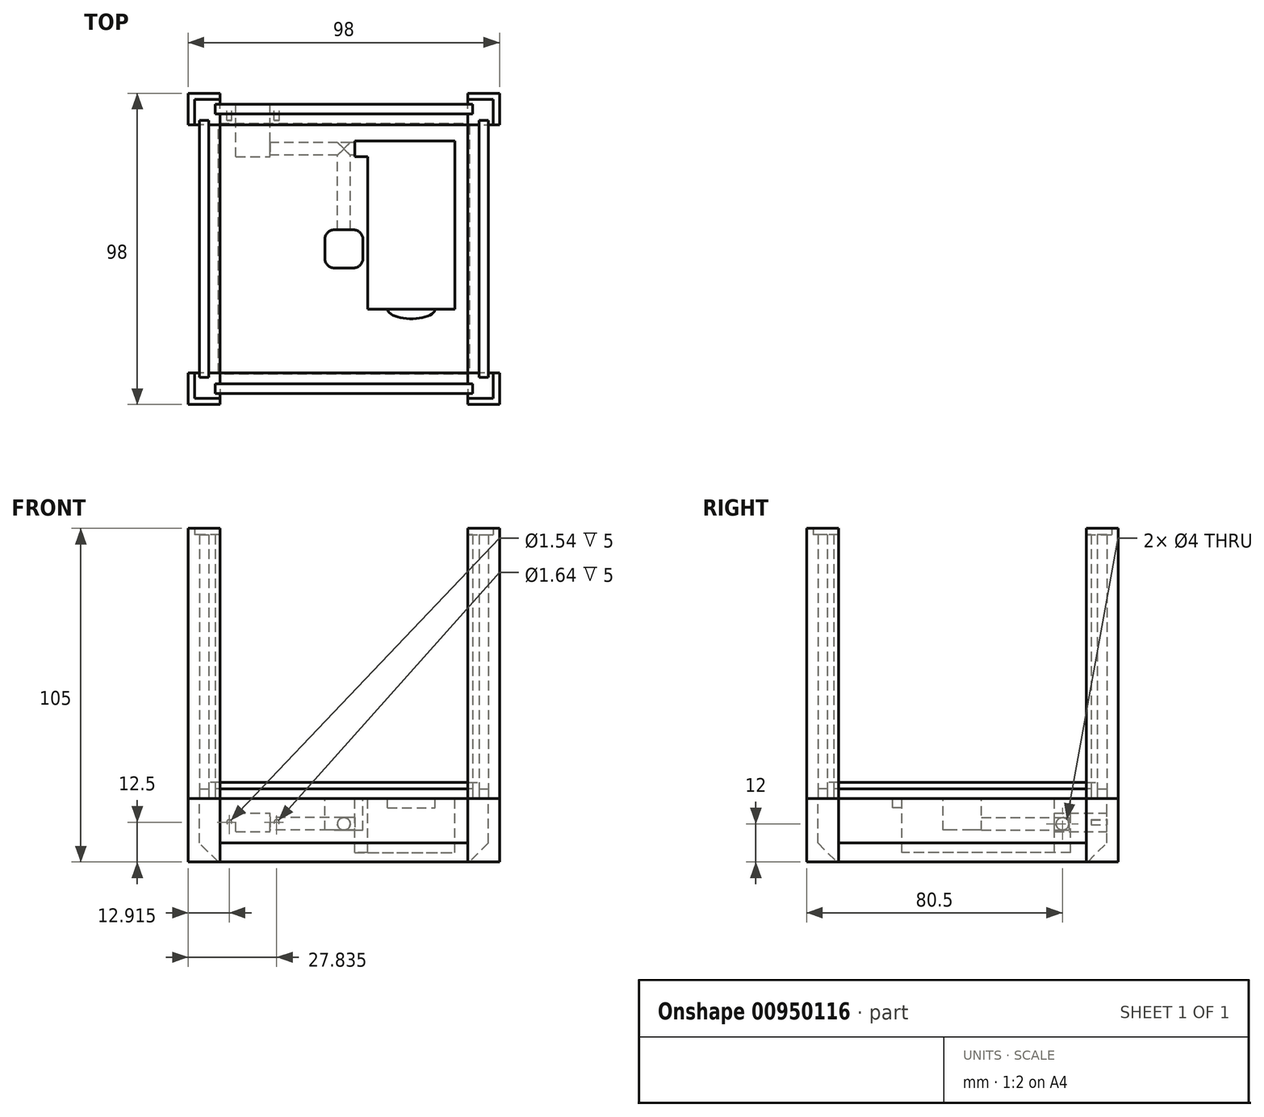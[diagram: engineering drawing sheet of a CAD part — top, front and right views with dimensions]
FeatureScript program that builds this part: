
annotation { "Feature Type Name" : "Feature", "Feature Type Description" : "" }
export const myFeature = defineFeature(function(context is Context, id is Id, definition is map)
    precondition{}
    {
        {
            var Q0;
            Q0=qCreatedBy(makeId("Top.planeOp"),FACE);
            var sketch = newSketch(context, id + "F0", { "sketchPlane" : qUnion([Q0])});
            skLineSegment(sketch, "E0.bottom", {"start": v(44, 44) * mm, "end": v(-44, 44) * mm});
            skLineSegment(sketch, "E0.top", {"start": v(44, -44) * mm, "end": v(-44, -44) * mm});
            skLineSegment(sketch, "E0.left", {"start": v(44, 44) * mm, "end": v(44, -44) * mm});
            skLineSegment(sketch, "E0.right", {"start": v(-44, 44) * mm, "end": v(-44, -44) * mm});
            skPoint(sketch, "E0.middle", {"position": v(0, 0) * mm});
            skLineSegment(sketch, "E1.bottom", {"start": v(39, 39) * mm, "end": v(49, 39) * mm});
            skLineSegment(sketch, "E1.top", {"start": v(39, 49) * mm, "end": v(49, 49) * mm});
            skLineSegment(sketch, "E1.left", {"start": v(39, 39) * mm, "end": v(39, 49) * mm});
            skLineSegment(sketch, "E1.right", {"start": v(49, 39) * mm, "end": v(49, 49) * mm});
            skPoint(sketch, "E1.middle", {"position": v(44, 44) * mm});
            skLineSegment(sketch, "E2.bottom", {"start": v(49, -39) * mm, "end": v(39, -39) * mm});
            skLineSegment(sketch, "E2.top", {"start": v(49, -49) * mm, "end": v(39, -49) * mm});
            skLineSegment(sketch, "E2.left", {"start": v(49, -39) * mm, "end": v(49, -49) * mm});
            skLineSegment(sketch, "E2.right", {"start": v(39, -39) * mm, "end": v(39, -49) * mm});
            skPoint(sketch, "E2.middle", {"position": v(44, -44) * mm});
            skLineSegment(sketch, "E3.bottom", {"start": v(-39, -39) * mm, "end": v(-49, -39) * mm});
            skLineSegment(sketch, "E3.top", {"start": v(-39, -49) * mm, "end": v(-49, -49) * mm});
            skLineSegment(sketch, "E3.left", {"start": v(-39, -39) * mm, "end": v(-39, -49) * mm});
            skLineSegment(sketch, "E3.right", {"start": v(-49, -39) * mm, "end": v(-49, -49) * mm});
            skPoint(sketch, "E3.middle", {"position": v(-44, -44) * mm});
            skLineSegment(sketch, "E4.bottom", {"start": v(-39, 39) * mm, "end": v(-49, 39) * mm});
            skLineSegment(sketch, "E4.top", {"start": v(-39, 49) * mm, "end": v(-49, 49) * mm});
            skLineSegment(sketch, "E4.left", {"start": v(-39, 39) * mm, "end": v(-39, 49) * mm});
            skLineSegment(sketch, "E4.right", {"start": v(-49, 39) * mm, "end": v(-49, 49) * mm});
            skPoint(sketch, "E4.middle", {"position": v(-44, 44) * mm});
            skLineSegment(sketch, "E5.0", {"start": v(45.5, 45.5) * mm, "end": v(45.5, -45.5) * mm});
            skLineSegment(sketch, "E5.1", {"start": v(45.5, 45.5) * mm, "end": v(-45.5, 45.5) * mm});
            skLineSegment(sketch, "E5.2", {"start": v(-45.5, 45.5) * mm, "end": v(-45.5, -45.5) * mm});
            skLineSegment(sketch, "E5.3", {"start": v(45.5, -45.5) * mm, "end": v(-45.5, -45.5) * mm});
            skLineSegment(sketch, "E6.0", {"start": v(42.5, 42.5) * mm, "end": v(42.5, -42.5) * mm});
            skLineSegment(sketch, "E6.1", {"start": v(42.5, 42.5) * mm, "end": v(-42.5, 42.5) * mm});
            skLineSegment(sketch, "E6.2", {"start": v(-42.5, 42.5) * mm, "end": v(-42.5, -42.5) * mm});
            skLineSegment(sketch, "E6.3", {"start": v(42.5, -42.5) * mm, "end": v(-42.5, -42.5) * mm});
            skLineSegment(sketch, "E7", {"start": v(42.5, 40.5) * mm, "end": v(45.5, 40.5) * mm});
            skLineSegment(sketch, "E8", {"start": v(40.5, 45.5) * mm, "end": v(40.5, 42.5) * mm});
            skLineSegment(sketch, "E9", {"start": v(42.5, -40.5) * mm, "end": v(45.5, -40.5) * mm});
            skLineSegment(sketch, "E10", {"start": v(40.5, -42.5) * mm, "end": v(40.5, -45.5) * mm});
            skLineSegment(sketch, "E11", {"start": v(-45.5, -40.5) * mm, "end": v(-42.5, -40.5) * mm});
            skLineSegment(sketch, "E12", {"start": v(-40.5, -42.5) * mm, "end": v(-40.5, -45.5) * mm});
            skLineSegment(sketch, "E13", {"start": v(-45.5, 40.5) * mm, "end": v(-42.5, 40.5) * mm});
            skLineSegment(sketch, "E14", {"start": v(-40.5, 42.5) * mm, "end": v(-40.5, 45.5) * mm});
            skLineSegment(sketch, "E15.0", {"start": v(39, 39) * mm, "end": v(-39, 39) * mm});
            skLineSegment(sketch, "E15.1", {"start": v(39, 39) * mm, "end": v(39, -39) * mm});
            skLineSegment(sketch, "E15.2", {"start": v(39, -39) * mm, "end": v(-39, -39) * mm});
            skLineSegment(sketch, "E15.3", {"start": v(-39, 39) * mm, "end": v(-39, -39) * mm});
            skSolve(sketch);
        }
        {
            var Q0;
            {var subQ0=sQuery(id+"F0.wireOp",EDGE,"E15.3");Q0=makeQuery(id+"F0.imprint","IMPRINT",FACE,{"disambiguationData":[TD([[makeQuery(id+"F0.imprint","IMPRINT",EDGE,{"derivedFrom":subQ0}),-1.0]])]});}
            var Q1;
            {var subQ0=sQuery(id+"F0.wireOp",EDGE,"E15.0");Q1=makeQuery(id+"F0.imprint","IMPRINT",FACE,{"disambiguationData":[TD([[makeQuery(id+"F0.imprint","IMPRINT",EDGE,{"derivedFrom":subQ0}),-1.0]])]});}
            var Q2;
            {var subQ0=sQuery(id+"F0.wireOp",EDGE,"E15.1");Q2=makeQuery(id+"F0.imprint","IMPRINT",FACE,{"disambiguationData":[TD([[makeQuery(id+"F0.imprint","IMPRINT",EDGE,{"derivedFrom":subQ0}),1.0]])]});}
            var Q3;
            {var subQ0=sQuery(id+"F0.wireOp",EDGE,"E15.2");Q3=makeQuery(id+"F0.imprint","IMPRINT",FACE,{"disambiguationData":[TD([[makeQuery(id+"F0.imprint","IMPRINT",EDGE,{"derivedFrom":subQ0}),1.0]])]});}
            extrude(context, id + "F1", {"entities" : qUnion([Q0, Q1, Q2, Q3]), "depth" : 5 * mm, "offsetDistance" : 25 * mm});
        }
        {
            var Q0;
            {var subQ1=sQuery(id+"F0.wireOp",EDGE,"E6.1");var subQ3=makeQuery(id+"F0.imprint","INTERSECT",VERTEX,{"derivedFrom":[subQ1,sQuery(id+"F0.wireOp",EDGE,"E14")]});Q0=makeQuery(id+"F0.imprint","IMPRINT",FACE,{"disambiguationData":[TD([[makeQuery(id+"F0.imprint","IMPRINT",EDGE,{"disambiguationData":[TD([[subQ3,1.0]])],"derivedFrom":subQ1}),1.0]])]});}
            var Q1;
            {var subQ5=sQuery(id+"F0.wireOp",EDGE,"E0.right");var subQ6=sQuery(id+"F0.wireOp",EDGE,"E0.bottom");var subQ7=makeQuery(id+"F0.imprint","INTERSECT",VERTEX,{"derivedFrom":[subQ6,subQ5]});Q1=makeQuery(id+"F0.imprint","IMPRINT",FACE,{"disambiguationData":[TD([[makeQuery(id+"F0.imprint","IMPRINT",EDGE,{"disambiguationData":[TD([[subQ7,1.0]])],"derivedFrom":subQ6}),1.0]])]});}
            var Q2;
            {var subQ5=sQuery(id+"F0.wireOp",EDGE,"E0.right");var subQ6=sQuery(id+"F0.wireOp",EDGE,"E0.bottom");var subQ7=makeQuery(id+"F0.imprint","INTERSECT",VERTEX,{"derivedFrom":[subQ6,subQ5]});Q2=makeQuery(id+"F0.imprint","IMPRINT",FACE,{"disambiguationData":[TD([[makeQuery(id+"F0.imprint","IMPRINT",EDGE,{"disambiguationData":[TD([[subQ7,1.0]])],"derivedFrom":subQ6}),-1.0]])]});}
            var Q3;
            {var subQ5=sQuery(id+"F0.wireOp",EDGE,"E4.top");Q3=makeQuery(id+"F0.imprint","IMPRINT",FACE,{"disambiguationData":[TD([[makeQuery(id+"F0.imprint","IMPRINT",EDGE,{"derivedFrom":subQ5}),1.0]])]});}
            var Q4;
            {var subQ1=sQuery(id+"F0.wireOp",EDGE,"E1.top");Q4=makeQuery(id+"F0.imprint","IMPRINT",FACE,{"disambiguationData":[TD([[makeQuery(id+"F0.imprint","IMPRINT",EDGE,{"derivedFrom":subQ1}),-1.0]])]});}
            var Q5;
            {var subQ5=sQuery(id+"F0.wireOp",EDGE,"E0.left");var subQ6=sQuery(id+"F0.wireOp",EDGE,"E0.bottom");var subQ7=makeQuery(id+"F0.imprint","INTERSECT",VERTEX,{"derivedFrom":[subQ6,subQ5]});Q5=makeQuery(id+"F0.imprint","IMPRINT",FACE,{"disambiguationData":[TD([[makeQuery(id+"F0.imprint","IMPRINT",EDGE,{"disambiguationData":[TD([[subQ7,-1.0]])],"derivedFrom":subQ6}),-1.0]])]});}
            var Q6;
            {var subQ7=sQuery(id+"F0.wireOp",EDGE,"E0.left");var subQ8=sQuery(id+"F0.wireOp",EDGE,"E0.bottom");var subQ9=makeQuery(id+"F0.imprint","INTERSECT",VERTEX,{"derivedFrom":[subQ8,subQ7]});Q6=makeQuery(id+"F0.imprint","IMPRINT",FACE,{"disambiguationData":[TD([[makeQuery(id+"F0.imprint","IMPRINT",EDGE,{"disambiguationData":[TD([[subQ9,-1.0]])],"derivedFrom":subQ8}),1.0]])]});}
            var Q7;
            {var subQ0=sQuery(id+"F0.wireOp",EDGE,"E6.0");var subQ4=sQuery(id+"F0.wireOp",EDGE,"E6.1");var subQ5=makeQuery(id+"F0.imprint","INTERSECT",VERTEX,{"derivedFrom":[subQ0,subQ4]});Q7=makeQuery(id+"F0.imprint","IMPRINT",FACE,{"disambiguationData":[TD([[makeQuery(id+"F0.imprint","IMPRINT",EDGE,{"disambiguationData":[TD([[subQ5,-1.0]])],"derivedFrom":subQ0}),-1.0]])]});}
            var Q8;
            {var subQ1=sQuery(id+"F0.wireOp",EDGE,"E2.top");Q8=makeQuery(id+"F0.imprint","IMPRINT",FACE,{"disambiguationData":[TD([[makeQuery(id+"F0.imprint","IMPRINT",EDGE,{"derivedFrom":subQ1}),-1.0]])]});}
            var Q9;
            {var subQ7=sQuery(id+"F0.wireOp",EDGE,"E0.left");var subQ8=sQuery(id+"F0.wireOp",EDGE,"E0.top");var subQ9=makeQuery(id+"F0.imprint","INTERSECT",VERTEX,{"derivedFrom":[subQ8,subQ7]});Q9=makeQuery(id+"F0.imprint","IMPRINT",FACE,{"disambiguationData":[TD([[makeQuery(id+"F0.imprint","IMPRINT",EDGE,{"disambiguationData":[TD([[subQ9,-1.0]])],"derivedFrom":subQ8}),1.0]])]});}
            var Q10;
            {var subQ7=sQuery(id+"F0.wireOp",EDGE,"E0.top");var subQ9=sQuery(id+"F0.wireOp",EDGE,"E0.left");var subQ10=makeQuery(id+"F0.imprint","INTERSECT",VERTEX,{"derivedFrom":[subQ7,subQ9]});Q10=makeQuery(id+"F0.imprint","IMPRINT",FACE,{"disambiguationData":[TD([[makeQuery(id+"F0.imprint","IMPRINT",EDGE,{"disambiguationData":[TD([[subQ10,-1.0]])],"derivedFrom":subQ7}),-1.0]])]});}
            var Q11;
            {var subQ1=sQuery(id+"F0.wireOp",EDGE,"E6.0");var subQ3=makeQuery(id+"F0.imprint","INTERSECT",VERTEX,{"derivedFrom":[subQ1,sQuery(id+"F0.wireOp",EDGE,"E9")]});Q11=makeQuery(id+"F0.imprint","IMPRINT",FACE,{"disambiguationData":[TD([[makeQuery(id+"F0.imprint","IMPRINT",EDGE,{"disambiguationData":[TD([[subQ3,1.0]])],"derivedFrom":subQ1}),-1.0]])]});}
            var Q12;
            {var subQ1=sQuery(id+"F0.wireOp",EDGE,"E6.2");var subQ3=makeQuery(id+"F0.imprint","INTERSECT",VERTEX,{"derivedFrom":[subQ1,sQuery(id+"F0.wireOp",EDGE,"E11")]});Q12=makeQuery(id+"F0.imprint","IMPRINT",FACE,{"disambiguationData":[TD([[makeQuery(id+"F0.imprint","IMPRINT",EDGE,{"disambiguationData":[TD([[subQ3,1.0]])],"derivedFrom":subQ1}),1.0]])]});}
            var Q13;
            {var subQ5=sQuery(id+"F0.wireOp",EDGE,"E0.top");var subQ9=sQuery(id+"F0.wireOp",EDGE,"E0.right");var subQ10=makeQuery(id+"F0.imprint","INTERSECT",VERTEX,{"derivedFrom":[subQ5,subQ9]});Q13=makeQuery(id+"F0.imprint","IMPRINT",FACE,{"disambiguationData":[TD([[makeQuery(id+"F0.imprint","IMPRINT",EDGE,{"disambiguationData":[TD([[subQ10,1.0]])],"derivedFrom":subQ5}),-1.0]])]});}
            var Q14;
            {var subQ7=sQuery(id+"F0.wireOp",EDGE,"E0.right");var subQ8=sQuery(id+"F0.wireOp",EDGE,"E0.top");var subQ9=makeQuery(id+"F0.imprint","INTERSECT",VERTEX,{"derivedFrom":[subQ8,subQ7]});Q14=makeQuery(id+"F0.imprint","IMPRINT",FACE,{"disambiguationData":[TD([[makeQuery(id+"F0.imprint","IMPRINT",EDGE,{"disambiguationData":[TD([[subQ9,1.0]])],"derivedFrom":subQ8}),1.0]])]});}
            var Q15;
            {var subQ1=sQuery(id+"F0.wireOp",EDGE,"E3.top");Q15=makeQuery(id+"F0.imprint","IMPRINT",FACE,{"disambiguationData":[TD([[makeQuery(id+"F0.imprint","IMPRINT",EDGE,{"derivedFrom":subQ1}),-1.0]])]});}
            extrude(context, id + "F2", {"entities" : qUnion([Q0, Q1, Q2, Q3, Q4, Q5, Q6, Q7, Q8, Q9, Q10, Q11, Q12, Q13, Q14, Q15]), "depth" : 83 * mm, "offsetDistance" : 25 * mm});
        }
        {
            var Q0;
            {var subQ0=sQuery(id+"F0.wireOp",EDGE,"E4.bottom");var subQ1=sQuery(id+"F0.wireOp",EDGE,"E0.right");var subQ2=makeQuery(id+"F0.imprint","INTERSECT",VERTEX,{"derivedFrom":[subQ1,subQ0]});Q0=makeQuery(id+"F0.imprint","IMPRINT",FACE,{"disambiguationData":[TD([[makeQuery(id+"F0.imprint","IMPRINT",EDGE,{"disambiguationData":[TD([[subQ2,-1.0]])],"derivedFrom":subQ1}),1.0]])]});}
            var Q1;
            {var subQ0=sQuery(id+"F0.wireOp",EDGE,"E4.bottom");var subQ1=sQuery(id+"F0.wireOp",EDGE,"E0.right");var subQ2=makeQuery(id+"F0.imprint","INTERSECT",VERTEX,{"derivedFrom":[subQ1,subQ0]});Q1=makeQuery(id+"F0.imprint","IMPRINT",FACE,{"disambiguationData":[TD([[makeQuery(id+"F0.imprint","IMPRINT",EDGE,{"disambiguationData":[TD([[subQ2,-1.0]])],"derivedFrom":subQ1}),-1.0]])]});}
            var Q2;
            {var subQ0=sQuery(id+"F0.wireOp",EDGE,"E13");var subQ1=sQuery(id+"F0.wireOp",EDGE,"E0.right");var subQ2=makeQuery(id+"F0.imprint","INTERSECT",VERTEX,{"derivedFrom":[subQ1,subQ0]});Q2=makeQuery(id+"F0.imprint","IMPRINT",FACE,{"disambiguationData":[TD([[makeQuery(id+"F0.imprint","IMPRINT",EDGE,{"disambiguationData":[TD([[subQ2,-1.0]])],"derivedFrom":subQ1}),1.0]])]});}
            var Q3;
            {var subQ0=sQuery(id+"F0.wireOp",EDGE,"E13");var subQ1=sQuery(id+"F0.wireOp",EDGE,"E0.right");var subQ2=makeQuery(id+"F0.imprint","INTERSECT",VERTEX,{"derivedFrom":[subQ1,subQ0]});Q3=makeQuery(id+"F0.imprint","IMPRINT",FACE,{"disambiguationData":[TD([[makeQuery(id+"F0.imprint","IMPRINT",EDGE,{"disambiguationData":[TD([[subQ2,-1.0]])],"derivedFrom":subQ1}),-1.0]])]});}
            var Q4;
            {var subQ0=sQuery(id+"F0.wireOp",EDGE,"E3.bottom");var subQ1=sQuery(id+"F0.wireOp",EDGE,"E0.right");var subQ2=makeQuery(id+"F0.imprint","INTERSECT",VERTEX,{"derivedFrom":[subQ1,subQ0]});Q4=makeQuery(id+"F0.imprint","IMPRINT",FACE,{"disambiguationData":[TD([[makeQuery(id+"F0.imprint","IMPRINT",EDGE,{"disambiguationData":[TD([[subQ2,-1.0]])],"derivedFrom":subQ1}),1.0]])]});}
            var Q5;
            {var subQ0=sQuery(id+"F0.wireOp",EDGE,"E3.bottom");var subQ1=sQuery(id+"F0.wireOp",EDGE,"E0.right");var subQ2=makeQuery(id+"F0.imprint","INTERSECT",VERTEX,{"derivedFrom":[subQ1,subQ0]});Q5=makeQuery(id+"F0.imprint","IMPRINT",FACE,{"disambiguationData":[TD([[makeQuery(id+"F0.imprint","IMPRINT",EDGE,{"disambiguationData":[TD([[subQ2,-1.0]])],"derivedFrom":subQ1}),-1.0]])]});}
            var Q6;
            {var subQ0=sQuery(id+"F0.wireOp",EDGE,"E2.right");var subQ1=sQuery(id+"F0.wireOp",EDGE,"E0.top");var subQ2=makeQuery(id+"F0.imprint","INTERSECT",VERTEX,{"derivedFrom":[subQ1,subQ0]});Q6=makeQuery(id+"F0.imprint","IMPRINT",FACE,{"disambiguationData":[TD([[makeQuery(id+"F0.imprint","IMPRINT",EDGE,{"disambiguationData":[TD([[subQ2,-1.0]])],"derivedFrom":subQ1}),-1.0]])]});}
            var Q7;
            {var subQ0=sQuery(id+"F0.wireOp",EDGE,"E3.left");var subQ1=sQuery(id+"F0.wireOp",EDGE,"E0.top");var subQ2=makeQuery(id+"F0.imprint","INTERSECT",VERTEX,{"derivedFrom":[subQ1,subQ0]});Q7=makeQuery(id+"F0.imprint","IMPRINT",FACE,{"disambiguationData":[TD([[makeQuery(id+"F0.imprint","IMPRINT",EDGE,{"disambiguationData":[TD([[subQ2,-1.0]])],"derivedFrom":subQ1}),-1.0]])]});}
            var Q8;
            {var subQ0=sQuery(id+"F0.wireOp",EDGE,"E3.left");var subQ1=sQuery(id+"F0.wireOp",EDGE,"E0.top");var subQ2=makeQuery(id+"F0.imprint","INTERSECT",VERTEX,{"derivedFrom":[subQ1,subQ0]});Q8=makeQuery(id+"F0.imprint","IMPRINT",FACE,{"disambiguationData":[TD([[makeQuery(id+"F0.imprint","IMPRINT",EDGE,{"disambiguationData":[TD([[subQ2,-1.0]])],"derivedFrom":subQ1}),1.0]])]});}
            var Q9;
            {var subQ0=sQuery(id+"F0.wireOp",EDGE,"E2.right");var subQ1=sQuery(id+"F0.wireOp",EDGE,"E0.top");var subQ2=makeQuery(id+"F0.imprint","INTERSECT",VERTEX,{"derivedFrom":[subQ1,subQ0]});Q9=makeQuery(id+"F0.imprint","IMPRINT",FACE,{"disambiguationData":[TD([[makeQuery(id+"F0.imprint","IMPRINT",EDGE,{"disambiguationData":[TD([[subQ2,-1.0]])],"derivedFrom":subQ1}),1.0]])]});}
            var Q10;
            {var subQ0=sQuery(id+"F0.wireOp",EDGE,"E10");var subQ1=sQuery(id+"F0.wireOp",EDGE,"E0.top");var subQ2=makeQuery(id+"F0.imprint","INTERSECT",VERTEX,{"derivedFrom":[subQ1,subQ0]});Q10=makeQuery(id+"F0.imprint","IMPRINT",FACE,{"disambiguationData":[TD([[makeQuery(id+"F0.imprint","IMPRINT",EDGE,{"disambiguationData":[TD([[subQ2,-1.0]])],"derivedFrom":subQ1}),1.0]])]});}
            var Q11;
            {var subQ0=sQuery(id+"F0.wireOp",EDGE,"E10");var subQ1=sQuery(id+"F0.wireOp",EDGE,"E0.top");var subQ2=makeQuery(id+"F0.imprint","INTERSECT",VERTEX,{"derivedFrom":[subQ1,subQ0]});Q11=makeQuery(id+"F0.imprint","IMPRINT",FACE,{"disambiguationData":[TD([[makeQuery(id+"F0.imprint","IMPRINT",EDGE,{"disambiguationData":[TD([[subQ2,-1.0]])],"derivedFrom":subQ1}),-1.0]])]});}
            var Q12;
            {var subQ0=sQuery(id+"F0.wireOp",EDGE,"E2.bottom");var subQ1=sQuery(id+"F0.wireOp",EDGE,"E0.left");var subQ2=makeQuery(id+"F0.imprint","INTERSECT",VERTEX,{"derivedFrom":[subQ1,subQ0]});Q12=makeQuery(id+"F0.imprint","IMPRINT",FACE,{"disambiguationData":[TD([[makeQuery(id+"F0.imprint","IMPRINT",EDGE,{"disambiguationData":[TD([[subQ2,-1.0]])],"derivedFrom":subQ1}),-1.0]])]});}
            var Q13;
            {var subQ0=sQuery(id+"F0.wireOp",EDGE,"E2.bottom");var subQ1=sQuery(id+"F0.wireOp",EDGE,"E0.left");var subQ2=makeQuery(id+"F0.imprint","INTERSECT",VERTEX,{"derivedFrom":[subQ1,subQ0]});Q13=makeQuery(id+"F0.imprint","IMPRINT",FACE,{"disambiguationData":[TD([[makeQuery(id+"F0.imprint","IMPRINT",EDGE,{"disambiguationData":[TD([[subQ2,-1.0]])],"derivedFrom":subQ1}),1.0]])]});}
            var Q14;
            {var subQ0=sQuery(id+"F0.wireOp",EDGE,"E1.bottom");var subQ1=sQuery(id+"F0.wireOp",EDGE,"E0.left");var subQ2=makeQuery(id+"F0.imprint","INTERSECT",VERTEX,{"derivedFrom":[subQ1,subQ0]});Q14=makeQuery(id+"F0.imprint","IMPRINT",FACE,{"disambiguationData":[TD([[makeQuery(id+"F0.imprint","IMPRINT",EDGE,{"disambiguationData":[TD([[subQ2,-1.0]])],"derivedFrom":subQ1}),1.0]])]});}
            var Q15;
            {var subQ0=sQuery(id+"F0.wireOp",EDGE,"E1.bottom");var subQ1=sQuery(id+"F0.wireOp",EDGE,"E0.left");var subQ2=makeQuery(id+"F0.imprint","INTERSECT",VERTEX,{"derivedFrom":[subQ1,subQ0]});Q15=makeQuery(id+"F0.imprint","IMPRINT",FACE,{"disambiguationData":[TD([[makeQuery(id+"F0.imprint","IMPRINT",EDGE,{"disambiguationData":[TD([[subQ2,-1.0]])],"derivedFrom":subQ1}),-1.0]])]});}
            var Q16;
            {var subQ0=sQuery(id+"F0.wireOp",EDGE,"E7");var subQ1=sQuery(id+"F0.wireOp",EDGE,"E0.left");var subQ2=makeQuery(id+"F0.imprint","INTERSECT",VERTEX,{"derivedFrom":[subQ1,subQ0]});Q16=makeQuery(id+"F0.imprint","IMPRINT",FACE,{"disambiguationData":[TD([[makeQuery(id+"F0.imprint","IMPRINT",EDGE,{"disambiguationData":[TD([[subQ2,-1.0]])],"derivedFrom":subQ1}),1.0]])]});}
            var Q17;
            {var subQ0=sQuery(id+"F0.wireOp",EDGE,"E7");var subQ1=sQuery(id+"F0.wireOp",EDGE,"E0.left");var subQ2=makeQuery(id+"F0.imprint","INTERSECT",VERTEX,{"derivedFrom":[subQ1,subQ0]});Q17=makeQuery(id+"F0.imprint","IMPRINT",FACE,{"disambiguationData":[TD([[makeQuery(id+"F0.imprint","IMPRINT",EDGE,{"disambiguationData":[TD([[subQ2,-1.0]])],"derivedFrom":subQ1}),-1.0]])]});}
            var Q18;
            {var subQ0=sQuery(id+"F0.wireOp",EDGE,"E8");var subQ1=sQuery(id+"F0.wireOp",EDGE,"E0.bottom");var subQ2=makeQuery(id+"F0.imprint","INTERSECT",VERTEX,{"derivedFrom":[subQ1,subQ0]});Q18=makeQuery(id+"F0.imprint","IMPRINT",FACE,{"disambiguationData":[TD([[makeQuery(id+"F0.imprint","IMPRINT",EDGE,{"disambiguationData":[TD([[subQ2,-1.0]])],"derivedFrom":subQ1}),1.0]])]});}
            var Q19;
            {var subQ0=sQuery(id+"F0.wireOp",EDGE,"E8");var subQ1=sQuery(id+"F0.wireOp",EDGE,"E0.bottom");var subQ2=makeQuery(id+"F0.imprint","INTERSECT",VERTEX,{"derivedFrom":[subQ1,subQ0]});Q19=makeQuery(id+"F0.imprint","IMPRINT",FACE,{"disambiguationData":[TD([[makeQuery(id+"F0.imprint","IMPRINT",EDGE,{"disambiguationData":[TD([[subQ2,-1.0]])],"derivedFrom":subQ1}),-1.0]])]});}
            var Q20;
            {var subQ0=sQuery(id+"F0.wireOp",EDGE,"E1.left");var subQ1=sQuery(id+"F0.wireOp",EDGE,"E0.bottom");var subQ2=makeQuery(id+"F0.imprint","INTERSECT",VERTEX,{"derivedFrom":[subQ1,subQ0]});Q20=makeQuery(id+"F0.imprint","IMPRINT",FACE,{"disambiguationData":[TD([[makeQuery(id+"F0.imprint","IMPRINT",EDGE,{"disambiguationData":[TD([[subQ2,-1.0]])],"derivedFrom":subQ1}),-1.0]])]});}
            var Q21;
            {var subQ0=sQuery(id+"F0.wireOp",EDGE,"E1.left");var subQ1=sQuery(id+"F0.wireOp",EDGE,"E0.bottom");var subQ2=makeQuery(id+"F0.imprint","INTERSECT",VERTEX,{"derivedFrom":[subQ1,subQ0]});Q21=makeQuery(id+"F0.imprint","IMPRINT",FACE,{"disambiguationData":[TD([[makeQuery(id+"F0.imprint","IMPRINT",EDGE,{"disambiguationData":[TD([[subQ2,-1.0]])],"derivedFrom":subQ1}),1.0]])]});}
            var Q22;
            {var subQ0=sQuery(id+"F0.wireOp",EDGE,"E4.left");var subQ1=sQuery(id+"F0.wireOp",EDGE,"E0.bottom");var subQ2=makeQuery(id+"F0.imprint","INTERSECT",VERTEX,{"derivedFrom":[subQ1,subQ0]});Q22=makeQuery(id+"F0.imprint","IMPRINT",FACE,{"disambiguationData":[TD([[makeQuery(id+"F0.imprint","IMPRINT",EDGE,{"disambiguationData":[TD([[subQ2,-1.0]])],"derivedFrom":subQ1}),1.0]])]});}
            var Q23;
            {var subQ0=sQuery(id+"F0.wireOp",EDGE,"E4.left");var subQ1=sQuery(id+"F0.wireOp",EDGE,"E0.bottom");var subQ2=makeQuery(id+"F0.imprint","INTERSECT",VERTEX,{"derivedFrom":[subQ1,subQ0]});Q23=makeQuery(id+"F0.imprint","IMPRINT",FACE,{"disambiguationData":[TD([[makeQuery(id+"F0.imprint","IMPRINT",EDGE,{"disambiguationData":[TD([[subQ2,-1.0]])],"derivedFrom":subQ1}),-1.0]])]});}
            extrude(context, id + "F3", {"entities" : qUnion([Q0, Q1, Q2, Q3, Q4, Q5, Q6, Q7, Q8, Q9, Q10, Q11, Q12, Q13, Q14, Q15, Q16, Q17, Q18, Q19, Q20, Q21, Q22, Q23]), "depth" : 3 * mm, "offsetDistance" : 25 * mm});
        }
        {
            var Q0;
            {var subQ0=sQuery(id+"F0.wireOp",EDGE,"E1.left");var subQ1=sQuery(id+"F0.wireOp",EDGE,"E0.bottom");var subQ2=makeQuery(id+"F0.imprint","INTERSECT",VERTEX,{"derivedFrom":[subQ1,subQ0]});Q0=makeQuery(id+"F0.imprint","IMPRINT",FACE,{"disambiguationData":[TD([[makeQuery(id+"F0.imprint","IMPRINT",EDGE,{"disambiguationData":[TD([[subQ2,-1.0]])],"derivedFrom":subQ1}),-1.0]])]});}
            var Q1;
            {var subQ0=sQuery(id+"F0.wireOp",EDGE,"E2.right");var subQ1=sQuery(id+"F0.wireOp",EDGE,"E0.top");var subQ2=makeQuery(id+"F0.imprint","INTERSECT",VERTEX,{"derivedFrom":[subQ1,subQ0]});Q1=makeQuery(id+"F0.imprint","IMPRINT",FACE,{"disambiguationData":[TD([[makeQuery(id+"F0.imprint","IMPRINT",EDGE,{"disambiguationData":[TD([[subQ2,-1.0]])],"derivedFrom":subQ1}),1.0]])]});}
            var Q2;
            {var subQ0=sQuery(id+"F0.wireOp",EDGE,"E1.bottom");var subQ1=sQuery(id+"F0.wireOp",EDGE,"E0.left");var subQ2=makeQuery(id+"F0.imprint","INTERSECT",VERTEX,{"derivedFrom":[subQ1,subQ0]});Q2=makeQuery(id+"F0.imprint","IMPRINT",FACE,{"disambiguationData":[TD([[makeQuery(id+"F0.imprint","IMPRINT",EDGE,{"disambiguationData":[TD([[subQ2,-1.0]])],"derivedFrom":subQ1}),1.0]])]});}
            var Q3;
            {var subQ0=sQuery(id+"F0.wireOp",EDGE,"E4.bottom");var subQ1=sQuery(id+"F0.wireOp",EDGE,"E0.right");var subQ2=makeQuery(id+"F0.imprint","INTERSECT",VERTEX,{"derivedFrom":[subQ1,subQ0]});Q3=makeQuery(id+"F0.imprint","IMPRINT",FACE,{"disambiguationData":[TD([[makeQuery(id+"F0.imprint","IMPRINT",EDGE,{"disambiguationData":[TD([[subQ2,-1.0]])],"derivedFrom":subQ1}),-1.0]])]});}
            var Q4;
            {var subQ1=sQuery(id+"F0.wireOp",EDGE,"E1.top");Q4=makeQuery(id+"F0.imprint","IMPRINT",FACE,{"disambiguationData":[TD([[makeQuery(id+"F0.imprint","IMPRINT",EDGE,{"derivedFrom":subQ1}),-1.0]])]});}
            var Q5;
            {var subQ1=sQuery(id+"F0.wireOp",EDGE,"E2.top");Q5=makeQuery(id+"F0.imprint","IMPRINT",FACE,{"disambiguationData":[TD([[makeQuery(id+"F0.imprint","IMPRINT",EDGE,{"derivedFrom":subQ1}),-1.0]])]});}
            var Q6;
            {var subQ1=sQuery(id+"F0.wireOp",EDGE,"E3.top");Q6=makeQuery(id+"F0.imprint","IMPRINT",FACE,{"disambiguationData":[TD([[makeQuery(id+"F0.imprint","IMPRINT",EDGE,{"derivedFrom":subQ1}),-1.0]])]});}
            var Q7;
            {var subQ5=sQuery(id+"F0.wireOp",EDGE,"E4.top");Q7=makeQuery(id+"F0.imprint","IMPRINT",FACE,{"disambiguationData":[TD([[makeQuery(id+"F0.imprint","IMPRINT",EDGE,{"derivedFrom":subQ5}),1.0]])]});}
            var Q8;
            {var subQ0=sQuery(id+"F0.wireOp",EDGE,"E8");var subQ1=sQuery(id+"F0.wireOp",EDGE,"E0.bottom");var subQ2=makeQuery(id+"F0.imprint","INTERSECT",VERTEX,{"derivedFrom":[subQ1,subQ0]});Q8=makeQuery(id+"F0.imprint","IMPRINT",FACE,{"disambiguationData":[TD([[makeQuery(id+"F0.imprint","IMPRINT",EDGE,{"disambiguationData":[TD([[subQ2,-1.0]])],"derivedFrom":subQ1}),-1.0]])]});}
            var Q9;
            {var subQ0=sQuery(id+"F0.wireOp",EDGE,"E4.left");var subQ1=sQuery(id+"F0.wireOp",EDGE,"E0.bottom");var subQ2=makeQuery(id+"F0.imprint","INTERSECT",VERTEX,{"derivedFrom":[subQ1,subQ0]});Q9=makeQuery(id+"F0.imprint","IMPRINT",FACE,{"disambiguationData":[TD([[makeQuery(id+"F0.imprint","IMPRINT",EDGE,{"disambiguationData":[TD([[subQ2,-1.0]])],"derivedFrom":subQ1}),-1.0]])]});}
            var Q10;
            {var subQ0=sQuery(id+"F0.wireOp",EDGE,"E10");var subQ1=sQuery(id+"F0.wireOp",EDGE,"E0.top");var subQ2=makeQuery(id+"F0.imprint","INTERSECT",VERTEX,{"derivedFrom":[subQ1,subQ0]});Q10=makeQuery(id+"F0.imprint","IMPRINT",FACE,{"disambiguationData":[TD([[makeQuery(id+"F0.imprint","IMPRINT",EDGE,{"disambiguationData":[TD([[subQ2,-1.0]])],"derivedFrom":subQ1}),1.0]])]});}
            var Q11;
            {var subQ0=sQuery(id+"F0.wireOp",EDGE,"E3.left");var subQ1=sQuery(id+"F0.wireOp",EDGE,"E0.top");var subQ2=makeQuery(id+"F0.imprint","INTERSECT",VERTEX,{"derivedFrom":[subQ1,subQ0]});Q11=makeQuery(id+"F0.imprint","IMPRINT",FACE,{"disambiguationData":[TD([[makeQuery(id+"F0.imprint","IMPRINT",EDGE,{"disambiguationData":[TD([[subQ2,-1.0]])],"derivedFrom":subQ1}),1.0]])]});}
            var Q12;
            {var subQ0=sQuery(id+"F0.wireOp",EDGE,"E7");var subQ1=sQuery(id+"F0.wireOp",EDGE,"E0.left");var subQ2=makeQuery(id+"F0.imprint","INTERSECT",VERTEX,{"derivedFrom":[subQ1,subQ0]});Q12=makeQuery(id+"F0.imprint","IMPRINT",FACE,{"disambiguationData":[TD([[makeQuery(id+"F0.imprint","IMPRINT",EDGE,{"disambiguationData":[TD([[subQ2,-1.0]])],"derivedFrom":subQ1}),1.0]])]});}
            var Q13;
            {var subQ0=sQuery(id+"F0.wireOp",EDGE,"E2.bottom");var subQ1=sQuery(id+"F0.wireOp",EDGE,"E0.left");var subQ2=makeQuery(id+"F0.imprint","INTERSECT",VERTEX,{"derivedFrom":[subQ1,subQ0]});Q13=makeQuery(id+"F0.imprint","IMPRINT",FACE,{"disambiguationData":[TD([[makeQuery(id+"F0.imprint","IMPRINT",EDGE,{"disambiguationData":[TD([[subQ2,-1.0]])],"derivedFrom":subQ1}),1.0]])]});}
            var Q14;
            {var subQ0=sQuery(id+"F0.wireOp",EDGE,"E13");var subQ1=sQuery(id+"F0.wireOp",EDGE,"E0.right");var subQ2=makeQuery(id+"F0.imprint","INTERSECT",VERTEX,{"derivedFrom":[subQ1,subQ0]});Q14=makeQuery(id+"F0.imprint","IMPRINT",FACE,{"disambiguationData":[TD([[makeQuery(id+"F0.imprint","IMPRINT",EDGE,{"disambiguationData":[TD([[subQ2,-1.0]])],"derivedFrom":subQ1}),-1.0]])]});}
            var Q15;
            {var subQ0=sQuery(id+"F0.wireOp",EDGE,"E3.bottom");var subQ1=sQuery(id+"F0.wireOp",EDGE,"E0.right");var subQ2=makeQuery(id+"F0.imprint","INTERSECT",VERTEX,{"derivedFrom":[subQ1,subQ0]});Q15=makeQuery(id+"F0.imprint","IMPRINT",FACE,{"disambiguationData":[TD([[makeQuery(id+"F0.imprint","IMPRINT",EDGE,{"disambiguationData":[TD([[subQ2,-1.0]])],"derivedFrom":subQ1}),-1.0]])]});}
            var Q16;
            {var subQ0=sQuery(id+"F0.wireOp",EDGE,"E15.1");Q16=makeQuery(id+"F0.imprint","IMPRINT",FACE,{"disambiguationData":[TD([[makeQuery(id+"F0.imprint","IMPRINT",EDGE,{"derivedFrom":subQ0}),1.0]])]});}
            var Q17;
            {var subQ0=sQuery(id+"F0.wireOp",EDGE,"E2.right");var subQ1=sQuery(id+"F0.wireOp",EDGE,"E0.top");var subQ2=makeQuery(id+"F0.imprint","INTERSECT",VERTEX,{"derivedFrom":[subQ1,subQ0]});Q17=makeQuery(id+"F0.imprint","IMPRINT",FACE,{"disambiguationData":[TD([[makeQuery(id+"F0.imprint","IMPRINT",EDGE,{"disambiguationData":[TD([[subQ2,-1.0]])],"derivedFrom":subQ1}),-1.0]])]});}
            var Q18;
            {var subQ0=sQuery(id+"F0.wireOp",EDGE,"E15.0");Q18=makeQuery(id+"F0.imprint","IMPRINT",FACE,{"disambiguationData":[TD([[makeQuery(id+"F0.imprint","IMPRINT",EDGE,{"derivedFrom":subQ0}),-1.0]])]});}
            var Q19;
            {var subQ0=sQuery(id+"F0.wireOp",EDGE,"E15.2");Q19=makeQuery(id+"F0.imprint","IMPRINT",FACE,{"disambiguationData":[TD([[makeQuery(id+"F0.imprint","IMPRINT",EDGE,{"derivedFrom":subQ0}),1.0]])]});}
            var Q20;
            {var subQ0=sQuery(id+"F0.wireOp",EDGE,"E1.left");var subQ1=sQuery(id+"F0.wireOp",EDGE,"E0.bottom");var subQ2=makeQuery(id+"F0.imprint","INTERSECT",VERTEX,{"derivedFrom":[subQ1,subQ0]});Q20=makeQuery(id+"F0.imprint","IMPRINT",FACE,{"disambiguationData":[TD([[makeQuery(id+"F0.imprint","IMPRINT",EDGE,{"disambiguationData":[TD([[subQ2,-1.0]])],"derivedFrom":subQ1}),1.0]])]});}
            var Q21;
            {var subQ0=sQuery(id+"F0.wireOp",EDGE,"E15.3");Q21=makeQuery(id+"F0.imprint","IMPRINT",FACE,{"disambiguationData":[TD([[makeQuery(id+"F0.imprint","IMPRINT",EDGE,{"derivedFrom":subQ0}),-1.0]])]});}
            var Q22;
            Q22=makeQuery(id+"F0.imprint","IMPRINT",FACE,{"disambiguationData":[TD([[makeQuery(id+"F0.imprint","IMPRINT",EDGE,{"derivedFrom":sQuery(id+"F0.wireOp",EDGE,"E15.0")}),1.0]])]});
            var Q23;
            {var subQ1=sQuery(id+"F0.wireOp",EDGE,"E6.0");var subQ3=makeQuery(id+"F0.imprint","INTERSECT",VERTEX,{"derivedFrom":[subQ1,sQuery(id+"F0.wireOp",EDGE,"E9")]});Q23=makeQuery(id+"F0.imprint","IMPRINT",FACE,{"disambiguationData":[TD([[makeQuery(id+"F0.imprint","IMPRINT",EDGE,{"disambiguationData":[TD([[subQ3,1.0]])],"derivedFrom":subQ1}),-1.0]])]});}
            var Q24;
            {var subQ0=sQuery(id+"F0.wireOp",EDGE,"E7");var subQ1=sQuery(id+"F0.wireOp",EDGE,"E0.left");var subQ2=makeQuery(id+"F0.imprint","INTERSECT",VERTEX,{"derivedFrom":[subQ1,subQ0]});Q24=makeQuery(id+"F0.imprint","IMPRINT",FACE,{"disambiguationData":[TD([[makeQuery(id+"F0.imprint","IMPRINT",EDGE,{"disambiguationData":[TD([[subQ2,-1.0]])],"derivedFrom":subQ1}),-1.0]])]});}
            var Q25;
            {var subQ1=sQuery(id+"F0.wireOp",EDGE,"E6.2");var subQ3=makeQuery(id+"F0.imprint","INTERSECT",VERTEX,{"derivedFrom":[subQ1,sQuery(id+"F0.wireOp",EDGE,"E11")]});Q25=makeQuery(id+"F0.imprint","IMPRINT",FACE,{"disambiguationData":[TD([[makeQuery(id+"F0.imprint","IMPRINT",EDGE,{"disambiguationData":[TD([[subQ3,1.0]])],"derivedFrom":subQ1}),1.0]])]});}
            var Q26;
            {var subQ1=sQuery(id+"F0.wireOp",EDGE,"E6.1");var subQ3=makeQuery(id+"F0.imprint","INTERSECT",VERTEX,{"derivedFrom":[subQ1,sQuery(id+"F0.wireOp",EDGE,"E14")]});Q26=makeQuery(id+"F0.imprint","IMPRINT",FACE,{"disambiguationData":[TD([[makeQuery(id+"F0.imprint","IMPRINT",EDGE,{"disambiguationData":[TD([[subQ3,1.0]])],"derivedFrom":subQ1}),1.0]])]});}
            var Q27;
            {var subQ0=sQuery(id+"F0.wireOp",EDGE,"E1.bottom");var subQ1=sQuery(id+"F0.wireOp",EDGE,"E0.left");var subQ2=makeQuery(id+"F0.imprint","INTERSECT",VERTEX,{"derivedFrom":[subQ1,subQ0]});Q27=makeQuery(id+"F0.imprint","IMPRINT",FACE,{"disambiguationData":[TD([[makeQuery(id+"F0.imprint","IMPRINT",EDGE,{"disambiguationData":[TD([[subQ2,-1.0]])],"derivedFrom":subQ1}),-1.0]])]});}
            var Q28;
            {var subQ5=sQuery(id+"F0.wireOp",EDGE,"E0.right");var subQ6=sQuery(id+"F0.wireOp",EDGE,"E0.bottom");var subQ7=makeQuery(id+"F0.imprint","INTERSECT",VERTEX,{"derivedFrom":[subQ6,subQ5]});Q28=makeQuery(id+"F0.imprint","IMPRINT",FACE,{"disambiguationData":[TD([[makeQuery(id+"F0.imprint","IMPRINT",EDGE,{"disambiguationData":[TD([[subQ7,1.0]])],"derivedFrom":subQ6}),-1.0]])]});}
            var Q29;
            {var subQ5=sQuery(id+"F0.wireOp",EDGE,"E0.left");var subQ6=sQuery(id+"F0.wireOp",EDGE,"E0.bottom");var subQ7=makeQuery(id+"F0.imprint","INTERSECT",VERTEX,{"derivedFrom":[subQ6,subQ5]});Q29=makeQuery(id+"F0.imprint","IMPRINT",FACE,{"disambiguationData":[TD([[makeQuery(id+"F0.imprint","IMPRINT",EDGE,{"disambiguationData":[TD([[subQ7,-1.0]])],"derivedFrom":subQ6}),-1.0]])]});}
            var Q30;
            {var subQ7=sQuery(id+"F0.wireOp",EDGE,"E0.left");var subQ8=sQuery(id+"F0.wireOp",EDGE,"E0.top");var subQ9=makeQuery(id+"F0.imprint","INTERSECT",VERTEX,{"derivedFrom":[subQ8,subQ7]});Q30=makeQuery(id+"F0.imprint","IMPRINT",FACE,{"disambiguationData":[TD([[makeQuery(id+"F0.imprint","IMPRINT",EDGE,{"disambiguationData":[TD([[subQ9,-1.0]])],"derivedFrom":subQ8}),1.0]])]});}
            var Q31;
            {var subQ0=sQuery(id+"F0.wireOp",EDGE,"E4.bottom");var subQ1=sQuery(id+"F0.wireOp",EDGE,"E0.right");var subQ2=makeQuery(id+"F0.imprint","INTERSECT",VERTEX,{"derivedFrom":[subQ1,subQ0]});Q31=makeQuery(id+"F0.imprint","IMPRINT",FACE,{"disambiguationData":[TD([[makeQuery(id+"F0.imprint","IMPRINT",EDGE,{"disambiguationData":[TD([[subQ2,-1.0]])],"derivedFrom":subQ1}),1.0]])]});}
            var Q32;
            {var subQ7=sQuery(id+"F0.wireOp",EDGE,"E0.right");var subQ8=sQuery(id+"F0.wireOp",EDGE,"E0.top");var subQ9=makeQuery(id+"F0.imprint","INTERSECT",VERTEX,{"derivedFrom":[subQ8,subQ7]});Q32=makeQuery(id+"F0.imprint","IMPRINT",FACE,{"disambiguationData":[TD([[makeQuery(id+"F0.imprint","IMPRINT",EDGE,{"disambiguationData":[TD([[subQ9,1.0]])],"derivedFrom":subQ8}),1.0]])]});}
            var Q33;
            {var subQ0=sQuery(id+"F0.wireOp",EDGE,"E3.bottom");var subQ1=sQuery(id+"F0.wireOp",EDGE,"E0.right");var subQ2=makeQuery(id+"F0.imprint","INTERSECT",VERTEX,{"derivedFrom":[subQ1,subQ0]});Q33=makeQuery(id+"F0.imprint","IMPRINT",FACE,{"disambiguationData":[TD([[makeQuery(id+"F0.imprint","IMPRINT",EDGE,{"disambiguationData":[TD([[subQ2,-1.0]])],"derivedFrom":subQ1}),1.0]])]});}
            var Q34;
            {var subQ0=sQuery(id+"F0.wireOp",EDGE,"E13");var subQ1=sQuery(id+"F0.wireOp",EDGE,"E0.right");var subQ2=makeQuery(id+"F0.imprint","INTERSECT",VERTEX,{"derivedFrom":[subQ1,subQ0]});Q34=makeQuery(id+"F0.imprint","IMPRINT",FACE,{"disambiguationData":[TD([[makeQuery(id+"F0.imprint","IMPRINT",EDGE,{"disambiguationData":[TD([[subQ2,-1.0]])],"derivedFrom":subQ1}),1.0]])]});}
            var Q35;
            {var subQ0=sQuery(id+"F0.wireOp",EDGE,"E6.0");var subQ4=sQuery(id+"F0.wireOp",EDGE,"E6.1");var subQ5=makeQuery(id+"F0.imprint","INTERSECT",VERTEX,{"derivedFrom":[subQ0,subQ4]});Q35=makeQuery(id+"F0.imprint","IMPRINT",FACE,{"disambiguationData":[TD([[makeQuery(id+"F0.imprint","IMPRINT",EDGE,{"disambiguationData":[TD([[subQ5,-1.0]])],"derivedFrom":subQ0}),-1.0]])]});}
            var Q36;
            {var subQ0=sQuery(id+"F0.wireOp",EDGE,"E10");var subQ1=sQuery(id+"F0.wireOp",EDGE,"E0.top");var subQ2=makeQuery(id+"F0.imprint","INTERSECT",VERTEX,{"derivedFrom":[subQ1,subQ0]});Q36=makeQuery(id+"F0.imprint","IMPRINT",FACE,{"disambiguationData":[TD([[makeQuery(id+"F0.imprint","IMPRINT",EDGE,{"disambiguationData":[TD([[subQ2,-1.0]])],"derivedFrom":subQ1}),-1.0]])]});}
            var Q37;
            {var subQ0=sQuery(id+"F0.wireOp",EDGE,"E2.bottom");var subQ1=sQuery(id+"F0.wireOp",EDGE,"E0.left");var subQ2=makeQuery(id+"F0.imprint","INTERSECT",VERTEX,{"derivedFrom":[subQ1,subQ0]});Q37=makeQuery(id+"F0.imprint","IMPRINT",FACE,{"disambiguationData":[TD([[makeQuery(id+"F0.imprint","IMPRINT",EDGE,{"disambiguationData":[TD([[subQ2,-1.0]])],"derivedFrom":subQ1}),-1.0]])]});}
            var Q38;
            {var subQ0=sQuery(id+"F0.wireOp",EDGE,"E3.left");var subQ1=sQuery(id+"F0.wireOp",EDGE,"E0.top");var subQ2=makeQuery(id+"F0.imprint","INTERSECT",VERTEX,{"derivedFrom":[subQ1,subQ0]});Q38=makeQuery(id+"F0.imprint","IMPRINT",FACE,{"disambiguationData":[TD([[makeQuery(id+"F0.imprint","IMPRINT",EDGE,{"disambiguationData":[TD([[subQ2,-1.0]])],"derivedFrom":subQ1}),-1.0]])]});}
            var Q39;
            {var subQ0=sQuery(id+"F0.wireOp",EDGE,"E4.left");var subQ1=sQuery(id+"F0.wireOp",EDGE,"E0.bottom");var subQ2=makeQuery(id+"F0.imprint","INTERSECT",VERTEX,{"derivedFrom":[subQ1,subQ0]});Q39=makeQuery(id+"F0.imprint","IMPRINT",FACE,{"disambiguationData":[TD([[makeQuery(id+"F0.imprint","IMPRINT",EDGE,{"disambiguationData":[TD([[subQ2,-1.0]])],"derivedFrom":subQ1}),1.0]])]});}
            var Q40;
            {var subQ5=sQuery(id+"F0.wireOp",EDGE,"E0.right");var subQ6=sQuery(id+"F0.wireOp",EDGE,"E0.bottom");var subQ7=makeQuery(id+"F0.imprint","INTERSECT",VERTEX,{"derivedFrom":[subQ6,subQ5]});Q40=makeQuery(id+"F0.imprint","IMPRINT",FACE,{"disambiguationData":[TD([[makeQuery(id+"F0.imprint","IMPRINT",EDGE,{"disambiguationData":[TD([[subQ7,1.0]])],"derivedFrom":subQ6}),1.0]])]});}
            var Q41;
            {var subQ7=sQuery(id+"F0.wireOp",EDGE,"E0.left");var subQ8=sQuery(id+"F0.wireOp",EDGE,"E0.bottom");var subQ9=makeQuery(id+"F0.imprint","INTERSECT",VERTEX,{"derivedFrom":[subQ8,subQ7]});Q41=makeQuery(id+"F0.imprint","IMPRINT",FACE,{"disambiguationData":[TD([[makeQuery(id+"F0.imprint","IMPRINT",EDGE,{"disambiguationData":[TD([[subQ9,-1.0]])],"derivedFrom":subQ8}),1.0]])]});}
            var Q42;
            {var subQ0=sQuery(id+"F0.wireOp",EDGE,"E8");var subQ1=sQuery(id+"F0.wireOp",EDGE,"E0.bottom");var subQ2=makeQuery(id+"F0.imprint","INTERSECT",VERTEX,{"derivedFrom":[subQ1,subQ0]});Q42=makeQuery(id+"F0.imprint","IMPRINT",FACE,{"disambiguationData":[TD([[makeQuery(id+"F0.imprint","IMPRINT",EDGE,{"disambiguationData":[TD([[subQ2,-1.0]])],"derivedFrom":subQ1}),1.0]])]});}
            var Q43;
            {var subQ7=sQuery(id+"F0.wireOp",EDGE,"E0.top");var subQ9=sQuery(id+"F0.wireOp",EDGE,"E0.left");var subQ10=makeQuery(id+"F0.imprint","INTERSECT",VERTEX,{"derivedFrom":[subQ7,subQ9]});Q43=makeQuery(id+"F0.imprint","IMPRINT",FACE,{"disambiguationData":[TD([[makeQuery(id+"F0.imprint","IMPRINT",EDGE,{"disambiguationData":[TD([[subQ10,-1.0]])],"derivedFrom":subQ7}),-1.0]])]});}
            var Q44;
            {var subQ5=sQuery(id+"F0.wireOp",EDGE,"E0.top");var subQ9=sQuery(id+"F0.wireOp",EDGE,"E0.right");var subQ10=makeQuery(id+"F0.imprint","INTERSECT",VERTEX,{"derivedFrom":[subQ5,subQ9]});Q44=makeQuery(id+"F0.imprint","IMPRINT",FACE,{"disambiguationData":[TD([[makeQuery(id+"F0.imprint","IMPRINT",EDGE,{"disambiguationData":[TD([[subQ10,1.0]])],"derivedFrom":subQ5}),-1.0]])]});}
            extrude(context, id + "F4", {"entities" : qUnion([Q0, Q1, Q2, Q3, Q4, Q5, Q6, Q7, Q8, Q9, Q10, Q11, Q12, Q13, Q14, Q15, Q16, Q17, Q18, Q19, Q20, Q21, Q22, Q23, Q24, Q25, Q26, Q27, Q28, Q29, Q30, Q31, Q32, Q33, Q34, Q35, Q36, Q37, Q38, Q39, Q40, Q41, Q42, Q43, Q44]), "oppositeDirection" : true, "depth" : 20 * mm, "offsetDistance" : 25 * mm});
        }
        {
            var Q0;
            Q0=makeQuery(id+"F0.imprint","IMPRINT",FACE,{"disambiguationData":[TD([[makeQuery(id+"F0.imprint","IMPRINT",EDGE,{"derivedFrom":sQuery(id+"F0.wireOp",EDGE,"E15.0")}),1.0]])]});
            var sketch = newSketch(context, id + "F5", { "sketchPlane" : qUnion([Q0])});
            skLineSegment(sketch, "E16.bottom", {"start": v(7.5, 34) * mm, "end": v(35, 34) * mm});
            skLineSegment(sketch, "E16.top", {"start": v(7.5, -19) * mm, "end": v(35, -19) * mm});
            skLineSegment(sketch, "E16.left", {"start": v(7.5, 29) * mm, "end": v(7.5, -19) * mm});
            skLineSegment(sketch, "E16.right", {"start": v(35, 34) * mm, "end": v(35, -19) * mm});
            skLineSegment(sketch, "E17.bottom", {"start": v(7.5, 34) * mm, "end": v(3.5, 34) * mm});
            skLineSegment(sketch, "E17.top", {"start": v(7.5, 29) * mm, "end": v(3.5, 29) * mm});
            skLineSegment(sketch, "E17.right", {"start": v(3.5, 34) * mm, "end": v(3.5, 29) * mm});
            skCircle(sketch, "E18", {"center": v(3.25, 3.25) * mm, "radius": 2.75 * mm, "construction": true});
            skLineSegment(sketch, "E19.bottom", {"start": v(-6, 6) * mm, "end": v(6, 6) * mm});
            skLineSegment(sketch, "E19.top", {"start": v(-6, -6) * mm, "end": v(6, -6) * mm});
            skLineSegment(sketch, "E19.left", {"start": v(-6, 6) * mm, "end": v(-6, -6) * mm});
            skLineSegment(sketch, "E19.right", {"start": v(6, 6) * mm, "end": v(6, -6) * mm});
            skPoint(sketch, "E19.middle", {"position": v(0, 0) * mm});
            skEllipticalArc(sketch, "E20", {});
            const initialGuessF5  = {"E20": [0.02125, -0.019, 1, 0, 0.0075, 0.003, 3.141592653589793, 0]};
            skSetInitialGuess(sketch, initialGuessF5);
            skSolve(sketch);
        }
        {
            var Q0;
            Q0=makeQuery(id+"F5.imprint","IMPRINT",FACE,{"disambiguationData":[TD([[makeQuery(id+"F5.imprint","IMPRINT",EDGE,{"derivedFrom":sQuery(id+"F5.wireOp",EDGE,"E16.bottom")}),-1.0]])]});
            extrude(context, id + "F6", {"entities" : qUnion([Q0]), "operationType" : NewBodyOperationType.REMOVE, "oppositeDirection" : true, "depth" : 17 * mm, "offsetDistance" : 25 * mm});
        }
        {
            var Q0;
            Q0=makeQuery(id+"F5.imprint","IMPRINT",FACE,{"disambiguationData":[TD([[makeQuery(id+"F5.imprint","IMPRINT",EDGE,{"derivedFrom":sQuery(id+"F5.wireOp",EDGE,"E19.bottom")}),-1.0]])]});
            extrude(context, id + "F7", {"entities" : qUnion([Q0]), "operationType" : NewBodyOperationType.REMOVE, "oppositeDirection" : true, "depth" : 10 * mm, "offsetDistance" : 25 * mm});
        }
        {
            var Q0;
            {var subQ0=sQuery(id+"F5.wireOp",EDGE,"E20");Q0=makeQuery(id+"F5.imprint","IMPRINT",FACE,{"disambiguationData":[TD([[makeQuery(id+"F5.imprint","IMPRINT",EDGE,{"derivedFrom":subQ0}),1.0]])]});}
            extrude(context, id + "F8", {"entities" : qUnion([Q0]), "operationType" : NewBodyOperationType.REMOVE, "oppositeDirection" : true, "depth" : 3 * mm, "offsetDistance" : 25 * mm});
        }
        {
            var Q0;
            Q0=makeQuery(id+"FnZgVdZsGpXSGG8_1.boolean.opBoolean","COPY",EDGE,{"derivedFrom":makeQuery(id+"FnZgVdZsGpXSGG8_1.opExtrude","CAP_EDGE",EDGE,{"disambiguationData":[OSD([sQuery(id+"F5.wireOp",EDGE,"9yl14sEB-3ev1-at5A-U6a4-tNM12GpERhYh.left")])],"isStart":false})});
            var Q1;
            Q1=makeQuery(id+"FnZgVdZsGpXSGG8_1.boolean.opBoolean","COPY",EDGE,{"derivedFrom":makeQuery(id+"FnZgVdZsGpXSGG8_1.opExtrude","CAP_EDGE",EDGE,{"disambiguationData":[OSD([sQuery(id+"F5.wireOp",EDGE,"9yl14sEB-3ev1-at5A-U6a4-tNM12GpERhYh.right")])],"isStart":false})});
            var Q2;
            Q2=makeQuery(id+"F7.boolean.opBoolean","COPY",EDGE,{"derivedFrom":makeQuery(id+"F7.opExtrude","SWEPT_EDGE",EDGE,{"disambiguationData":[OSD([sQuery(id+"F5.wireOp",EDGE,"E19.bottom"),sQuery(id+"F5.wireOp",EDGE,"E19.right")])]})});
            var Q3;
            Q3=makeQuery(id+"F7.boolean.opBoolean","COPY",EDGE,{"derivedFrom":makeQuery(id+"F7.opExtrude","SWEPT_EDGE",EDGE,{"disambiguationData":[OSD([sQuery(id+"F5.wireOp",EDGE,"E19.top"),sQuery(id+"F5.wireOp",EDGE,"E19.right")])]})});
            var Q4;
            Q4=makeQuery(id+"F7.boolean.opBoolean","COPY",EDGE,{"derivedFrom":makeQuery(id+"F7.opExtrude","SWEPT_EDGE",EDGE,{"disambiguationData":[OSD([sQuery(id+"F5.wireOp",EDGE,"E19.top"),sQuery(id+"F5.wireOp",EDGE,"E19.left")])]})});
            var Q5;
            Q5=makeQuery(id+"F7.boolean.opBoolean","COPY",EDGE,{"derivedFrom":makeQuery(id+"F7.opExtrude","SWEPT_EDGE",EDGE,{"disambiguationData":[OSD([sQuery(id+"F5.wireOp",EDGE,"E19.bottom"),sQuery(id+"F5.wireOp",EDGE,"E19.left")])]})});
            fillet(context, id + "F9", {"entities" : qUnion([Q0, Q1, Q2, Q3, Q4, Q5]), "radius" : 3 * mm, "tangentPropagation" : true, "allowEdgeOverflow" : false});
        }
        {
            var Q0;
            Q0=makeQuery(id+"F4.opExtrude","CAP_EDGE",EDGE,{"disambiguationData":[OSD([sQuery(id+"F0.wireOp",EDGE,"E5.1")])],"isStart":false});
            var Q1;
            Q1=makeQuery(id+"F4.opExtrude","CAP_EDGE",EDGE,{"disambiguationData":[OSD([sQuery(id+"F0.wireOp",EDGE,"E5.2")])],"isStart":false});
            var Q2;
            Q2=makeQuery(id+"F4.opExtrude","CAP_EDGE",EDGE,{"disambiguationData":[OSD([sQuery(id+"F0.wireOp",EDGE,"E5.3")])],"isStart":false});
            var Q3;
            Q3=makeQuery(id+"F4.opExtrude","CAP_EDGE",EDGE,{"disambiguationData":[OSD([sQuery(id+"F0.wireOp",EDGE,"E5.0")])],"isStart":false});
            chamfer(context, id + "F10", {"entities" : qUnion([Q0, Q1, Q2, Q3]), "width" : 6 * mm, "tangentPropagation" : true});
        }
        {
            var Q0;
            Q0=makeQuery(id+"F2.opExtrude","CAP_FACE",FACE,{"disambiguationData":[OSD([sQuery(id+"F0.wireOp",EDGE,"E1.bottom"),sQuery(id+"F0.wireOp",EDGE,"E1.top"),sQuery(id+"F0.wireOp",EDGE,"E1.left"),sQuery(id+"F0.wireOp",EDGE,"E1.right"),sQuery(id+"F0.wireOp",EDGE,"E5.0"),sQuery(id+"F0.wireOp",EDGE,"E5.1"),sQuery(id+"F0.wireOp",EDGE,"E6.0"),sQuery(id+"F0.wireOp",EDGE,"E6.1"),sQuery(id+"F0.wireOp",EDGE,"E7"),sQuery(id+"F0.wireOp",EDGE,"E8")])],"isStart":false});
            var sketch = newSketch(context, id + "F11", { "sketchPlane" : qUnion([Q0])});
            skLineSegment(sketch, "E21.0", {"start": v(39, 47) * mm, "end": v(47, 47) * mm});
            skLineSegment(sketch, "E21.1", {"start": v(47, 39) * mm, "end": v(47, 47) * mm});
            skSolve(sketch);
        }
        {
            var Q0;
            Q0=makeQuery(id+"F2.opExtrude","CAP_FACE",FACE,{"disambiguationData":[OSD([sQuery(id+"F0.wireOp",EDGE,"E4.bottom"),sQuery(id+"F0.wireOp",EDGE,"E4.top"),sQuery(id+"F0.wireOp",EDGE,"E4.left"),sQuery(id+"F0.wireOp",EDGE,"E4.right"),sQuery(id+"F0.wireOp",EDGE,"E5.1"),sQuery(id+"F0.wireOp",EDGE,"E5.2"),sQuery(id+"F0.wireOp",EDGE,"E6.1"),sQuery(id+"F0.wireOp",EDGE,"E6.2"),sQuery(id+"F0.wireOp",EDGE,"E13"),sQuery(id+"F0.wireOp",EDGE,"E14")])],"isStart":false});
            var sketch = newSketch(context, id + "F12", { "sketchPlane" : qUnion([Q0])});
            skLineSegment(sketch, "E22.0", {"start": v(-39, 47) * mm, "end": v(-47, 47) * mm});
            skLineSegment(sketch, "E22.1", {"start": v(-47, 39) * mm, "end": v(-47, 47) * mm});
            skSolve(sketch);
        }
        {
            var Q0;
            Q0=makeQuery(id+"F2.opExtrude","CAP_FACE",FACE,{"disambiguationData":[OSD([sQuery(id+"F0.wireOp",EDGE,"E3.bottom"),sQuery(id+"F0.wireOp",EDGE,"E3.top"),sQuery(id+"F0.wireOp",EDGE,"E3.left"),sQuery(id+"F0.wireOp",EDGE,"E3.right"),sQuery(id+"F0.wireOp",EDGE,"E5.2"),sQuery(id+"F0.wireOp",EDGE,"E5.3"),sQuery(id+"F0.wireOp",EDGE,"E6.2"),sQuery(id+"F0.wireOp",EDGE,"E6.3"),sQuery(id+"F0.wireOp",EDGE,"E11"),sQuery(id+"F0.wireOp",EDGE,"E12")])],"isStart":false});
            var sketch = newSketch(context, id + "F13", { "sketchPlane" : qUnion([Q0])});
            skLineSegment(sketch, "E23.0", {"start": v(-39, -47) * mm, "end": v(-47, -47) * mm});
            skLineSegment(sketch, "E23.1", {"start": v(-47, -39) * mm, "end": v(-47, -47) * mm});
            skSolve(sketch);
        }
        {
            var Q0;
            Q0=makeQuery(id+"F2.opExtrude","CAP_FACE",FACE,{"disambiguationData":[OSD([sQuery(id+"F0.wireOp",EDGE,"E2.bottom"),sQuery(id+"F0.wireOp",EDGE,"E2.top"),sQuery(id+"F0.wireOp",EDGE,"E2.left"),sQuery(id+"F0.wireOp",EDGE,"E2.right"),sQuery(id+"F0.wireOp",EDGE,"E5.0"),sQuery(id+"F0.wireOp",EDGE,"E5.3"),sQuery(id+"F0.wireOp",EDGE,"E6.0"),sQuery(id+"F0.wireOp",EDGE,"E6.3"),sQuery(id+"F0.wireOp",EDGE,"E9"),sQuery(id+"F0.wireOp",EDGE,"E10")])],"isStart":false});
            var sketch = newSketch(context, id + "F14", { "sketchPlane" : qUnion([Q0])});
            skLineSegment(sketch, "E24.0", {"start": v(47, -47) * mm, "end": v(39, -47) * mm});
            skLineSegment(sketch, "E24.1", {"start": v(47, -39) * mm, "end": v(47, -47) * mm});
            skSolve(sketch);
        }
        {
            var Q0;
            {var subQ4=sQuery(id+"F12.wireOp",EDGE,"E22.0");Q0=makeQuery(id+"F12.imprint","IMPRINT",FACE,{"disambiguationData":[TD([[makeQuery(id+"F12.imprint","IMPRINT",EDGE,{"derivedFrom":subQ4}),-1.0]])]});}
            var Q1;
            {var subQ4=sQuery(id+"F11.wireOp",EDGE,"E21.0");Q1=makeQuery(id+"F11.imprint","IMPRINT",FACE,{"disambiguationData":[TD([[makeQuery(id+"F11.imprint","IMPRINT",EDGE,{"derivedFrom":subQ4}),1.0]])]});}
            var Q2;
            {var subQ6=sQuery(id+"F14.wireOp",EDGE,"E24.0");Q2=makeQuery(id+"F14.imprint","IMPRINT",FACE,{"disambiguationData":[TD([[makeQuery(id+"F14.imprint","IMPRINT",EDGE,{"derivedFrom":subQ6}),1.0]])]});}
            var Q3;
            {var subQ4=sQuery(id+"F13.wireOp",EDGE,"E23.0");Q3=makeQuery(id+"F13.imprint","IMPRINT",FACE,{"disambiguationData":[TD([[makeQuery(id+"F13.imprint","IMPRINT",EDGE,{"derivedFrom":subQ4}),1.0]])]});}
            extrude(context, id + "F15", {"entities" : qUnion([Q0, Q1, Q2, Q3]), "operationType" : NewBodyOperationType.ADD, "depth" : 2 * mm, "offsetDistance" : 25 * mm});
        }
        {
            var Q0;
            Q0=makeQuery(id+"F4.opExtrude","SWEPT_FACE",FACE,{"disambiguationData":[OSD([sQuery(id+"F0.wireOp",EDGE,"E5.1")])]});
            var sketch = newSketch(context, id + "F16", { "sketchPlane" : qUnion([Q0])});
            skLineSegment(sketch, "E25.bottom", {"start": v(34, -10.4) * mm, "end": v(23.25, -10.4) * mm});
            skLineSegment(sketch, "E25.top", {"start": v(34, -4.6) * mm, "end": v(23.25, -4.6) * mm});
            skLineSegment(sketch, "E25.left", {"start": v(34, -10.4) * mm, "end": v(34, -4.6) * mm});
            skLineSegment(sketch, "E25.right", {"start": v(23.25, -10.4) * mm, "end": v(23.25, -4.6) * mm});
            skCircle(sketch, "E26", {"center": v(21.16, -7.5) * mm, "radius": 1.02 * mm, "construction": true});
            skCircle(sketch, "E27", {"center": v(36.09, -7.5) * mm, "radius": 1.02 * mm, "construction": true});
            skPoint(sketch, "E27.centerSnap0", {"position": v(34, -7.5) * mm});
            skPoint(sketch, "E28", {"position": v(23.25, -7.5) * mm});
            skLineSegment(sketch, "E29.bottom", {"start": v(38.38, -5.25) * mm, "end": v(18.88, -5.25) * mm, "construction": true});
            skLineSegment(sketch, "E29.top", {"start": v(38.38, -9.75) * mm, "end": v(18.88, -9.75) * mm, "construction": true});
            skLineSegment(sketch, "E29.left", {"start": v(38.38, -5.25) * mm, "end": v(38.38, -9.75) * mm, "construction": true});
            skLineSegment(sketch, "E29.right", {"start": v(18.88, -5.25) * mm, "end": v(18.88, -9.75) * mm, "construction": true});
            skPoint(sketch, "E29.middle", {"position": v(28.62, -7.5) * mm});
            skPoint(sketch, "E29.middle.positionSnap0", {"position": v(28.63, -4.6) * mm});
            skPoint(sketch, "E29.centerSnap0", {"position": v(28.63, -4.6) * mm});
            skCircle(sketch, "E30.0", {"center": v(21.16, -7.5) * mm, "radius": 0.82 * mm});
            skCircle(sketch, "E31.0", {"center": v(36.09, -7.5) * mm, "radius": 0.77 * mm});
            skCircle(sketch, "E32", {"center": v(0, -8) * mm, "radius": 2 * mm});
            skSolve(sketch);
        }
        {
            var Q0;
            Q0=makeQuery(id+"F16.imprint","IMPRINT",FACE,{"disambiguationData":[TD([[makeQuery(id+"F16.imprint","IMPRINT",EDGE,{"derivedFrom":sQuery(id+"F16.wireOp",EDGE,"E25.bottom")}),-1.0]])]});
            extrude(context, id + "F17", {"entities" : qUnion([Q0]), "operationType" : NewBodyOperationType.REMOVE, "oppositeDirection" : true, "depth" : 16.5 * mm, "offsetDistance" : 25 * mm});
        }
        {
            var Q0;
            Q0=makeQuery(id+"F16.imprint","IMPRINT",FACE,{"disambiguationData":[TD([[makeQuery(id+"F16.imprint","IMPRINT",EDGE,{"derivedFrom":sQuery(id+"F16.wireOp",EDGE,"E30.0")}),1.0]])]});
            var Q1;
            Q1=makeQuery(id+"F16.imprint","IMPRINT",FACE,{"disambiguationData":[TD([[makeQuery(id+"F16.imprint","IMPRINT",EDGE,{"derivedFrom":sQuery(id+"F16.wireOp",EDGE,"E31.0")}),1.0]])]});
            extrude(context, id + "F18", {"entities" : qUnion([Q0, Q1]), "operationType" : NewBodyOperationType.REMOVE, "oppositeDirection" : true, "depth" : 5 * mm, "offsetDistance" : 25 * mm});
        }
        {
            var Q0;
            Q0=makeQuery(id+"F4.opExtrude","SWEPT_FACE",FACE,{"disambiguationData":[OSD([sQuery(id+"F0.wireOp",EDGE,"E5.2")])]});
            var sketch = newSketch(context, id + "F19", { "sketchPlane" : qUnion([Q0])});
            skCircle(sketch, "E33", {"center": v(-31.5, -8) * mm, "radius": 2 * mm});
            skSolve(sketch);
        }
        {
            var Q0;
            Q0=qSketchRegion(id+"F19",true);
            extrude(context, id + "F20", {"entities" : qUnion([Q0]), "operationType" : NewBodyOperationType.REMOVE, "oppositeDirection" : true, "depth" : 50 * mm, "offsetDistance" : 25 * mm});
        }
        {
            var Q0;
            Q0=makeQuery(id+"F19.imprint","IMPRINT",FACE,{"disambiguationData":[TD([[makeQuery(id+"F19.imprint","IMPRINT",EDGE,{"derivedFrom":sQuery(id+"F19.wireOp",EDGE,"E33")}),1.0]])]});
            extrude(context, id + "F21", {"entities" : qUnion([Q0]), "operationType" : NewBodyOperationType.ADD, "oppositeDirection" : true, "depth" : 11.5 * mm, "offsetDistance" : 25 * mm});
        }
        {
            var Q0;
            Q0=makeQuery(id+"F16.imprint","IMPRINT",FACE,{"disambiguationData":[TD([[makeQuery(id+"F16.imprint","IMPRINT",EDGE,{"derivedFrom":sQuery(id+"F16.wireOp",EDGE,"E32")}),1.0]])]});
            extrude(context, id + "F22", {"entities" : qUnion([Q0]), "operationType" : NewBodyOperationType.REMOVE, "oppositeDirection" : true, "depth" : 41.6 * mm, "offsetDistance" : 25 * mm});
        }
        {
            var Q0;
            Q0=makeQuery(id+"F16.imprint","IMPRINT",FACE,{"disambiguationData":[TD([[makeQuery(id+"F16.imprint","IMPRINT",EDGE,{"derivedFrom":sQuery(id+"F16.wireOp",EDGE,"E32")}),1.0]])]});
            extrude(context, id + "F23", {"entities" : qUnion([Q0]), "operationType" : NewBodyOperationType.ADD, "oppositeDirection" : true, "depth" : 12 * mm, "offsetDistance" : 25 * mm});
        }
    });
